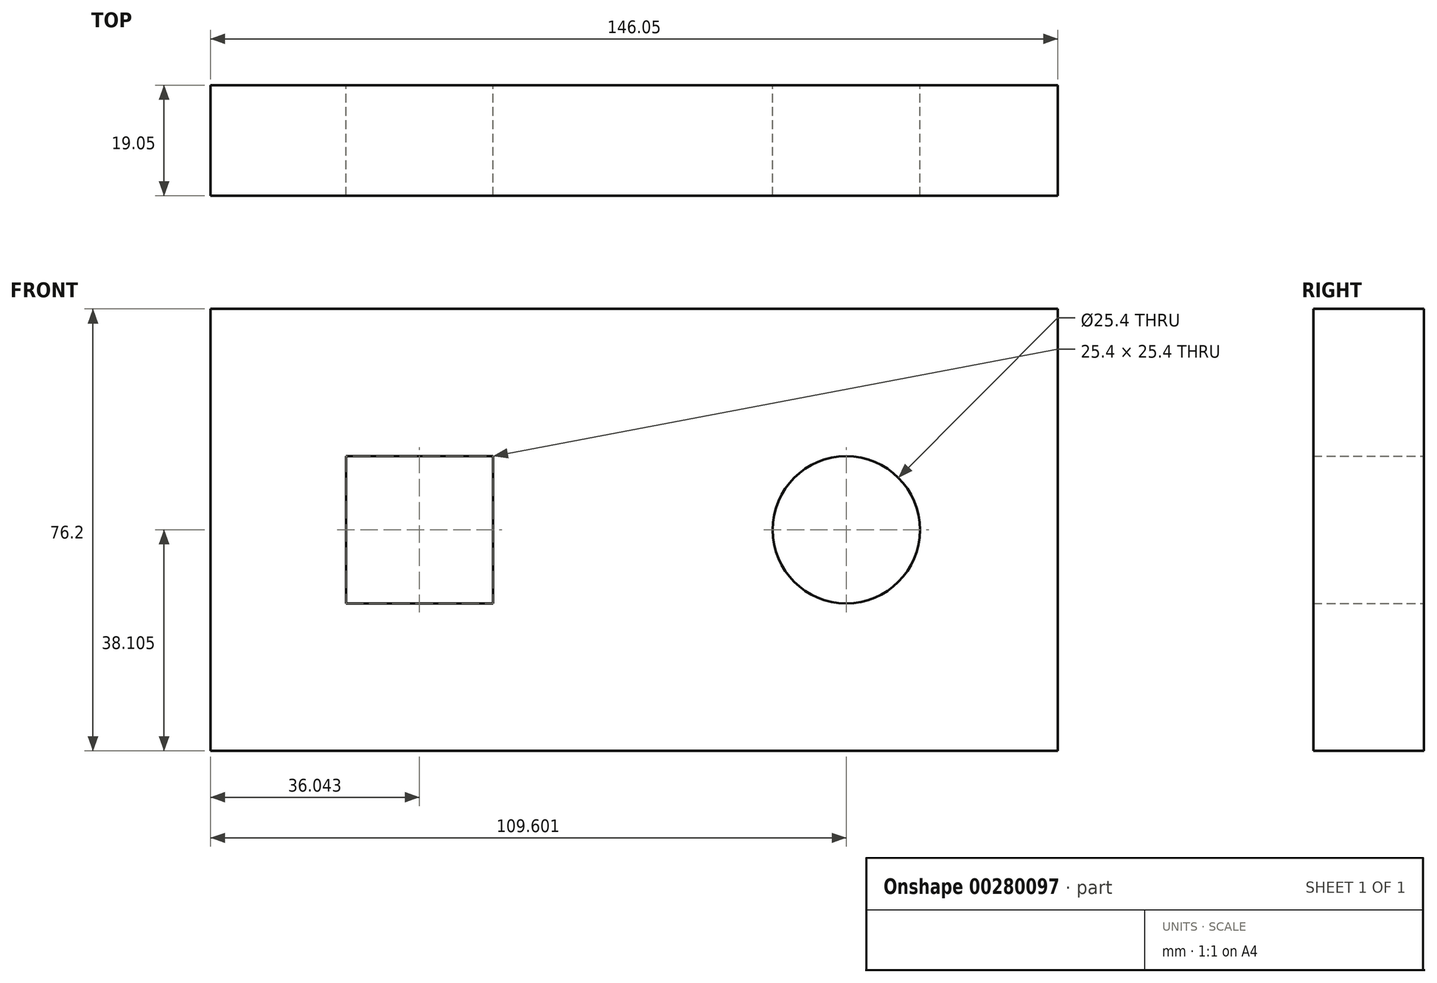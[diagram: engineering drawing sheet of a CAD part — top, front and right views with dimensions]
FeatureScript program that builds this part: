
annotation { "Feature Type Name" : "Feature", "Feature Type Description" : "" }
export const myFeature = defineFeature(function(context is Context, id is Id, definition is map)
    precondition{}
    {
        {
            var Q0;
            Q0=qCreatedBy(makeId("Front.planeOp"),FACE);
            var sketch = newSketch(context, id + "F0", { "sketchPlane" : qUnion([Q0])});
            skLineSegment(sketch, "E0.bottom", {"start": v(0, -1.75) * mm, "end": v(-146.05, -1.75) * mm});
            skLineSegment(sketch, "E0.top", {"start": v(0, 74.45) * mm, "end": v(-146.05, 74.45) * mm});
            skLineSegment(sketch, "E0.left", {"start": v(0, -1.75) * mm, "end": v(0, 74.45) * mm});
            skLineSegment(sketch, "E0.right", {"start": v(-146.05, -1.75) * mm, "end": v(-146.05, 74.45) * mm});
            skCircle(sketch, "E1", {"center": v(-36.45, 36.35) * mm, "radius": 12.7 * mm});
            skLineSegment(sketch, "E2.bottom", {"start": v(-122.7, 49.05) * mm, "end": v(-97.3, 49.05) * mm});
            skLineSegment(sketch, "E2.top", {"start": v(-122.7, 23.65) * mm, "end": v(-97.3, 23.65) * mm});
            skLineSegment(sketch, "E2.left", {"start": v(-122.7, 49.05) * mm, "end": v(-122.7, 23.65) * mm});
            skLineSegment(sketch, "E2.right", {"start": v(-97.3, 49.05) * mm, "end": v(-97.3, 23.65) * mm});
            skSolve(sketch);
        }
        {
            var Q0;
            Q0 = qSketchRegion(id + "F0", true);
            extrude(context, id + "F1", {"entities" : qUnion([Q0]), "depth" : 19.05 * mm});
        }
    });
